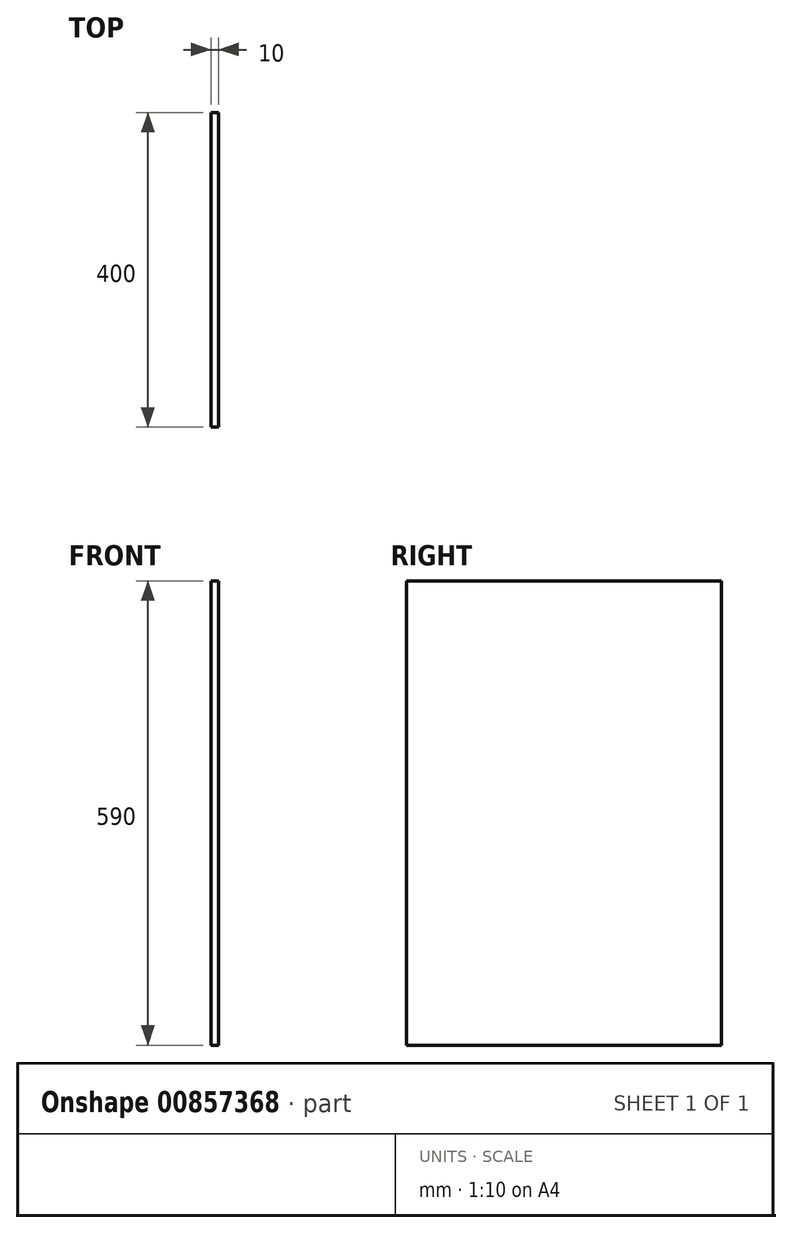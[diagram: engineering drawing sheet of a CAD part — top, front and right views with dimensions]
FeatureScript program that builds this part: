
annotation { "Feature Type Name" : "Feature", "Feature Type Description" : "" }
export const myFeature = defineFeature(function(context is Context, id is Id, definition is map)
    precondition{}
    {
        {
            var Q0;
            Q0=qCreatedBy(makeId("Right.planeOp"),FACE);
            var sketch = newSketch(context, id + "F0", { "sketchPlane" : qUnion([Q0])});
            skLineSegment(sketch, "E0.bottom", {"start": v(200, 295) * mm, "end": v(-200, 295) * mm});
            skLineSegment(sketch, "E0.top", {"start": v(200, -295) * mm, "end": v(-200, -295) * mm});
            skLineSegment(sketch, "E0.left", {"start": v(200, 295) * mm, "end": v(200, -295) * mm});
            skLineSegment(sketch, "E0.right", {"start": v(-200, 295) * mm, "end": v(-200, -295) * mm});
            skSolve(sketch);
        }
        {
            var Q0;
            Q0=makeQuery(id+"F0.imprint","IMPRINT",FACE,{"disambiguationData":[TD([[makeQuery(id+"F0.imprint","IMPRINT",EDGE,{"derivedFrom":sQuery(id+"F0.wireOp",EDGE,"E0.bottom")}),1.0]])]});
            extrude(context, id + "F1", {"entities" : qUnion([Q0]), "depth" : 10 * mm, "offsetDistance" : 25 * mm});
        }
    });
